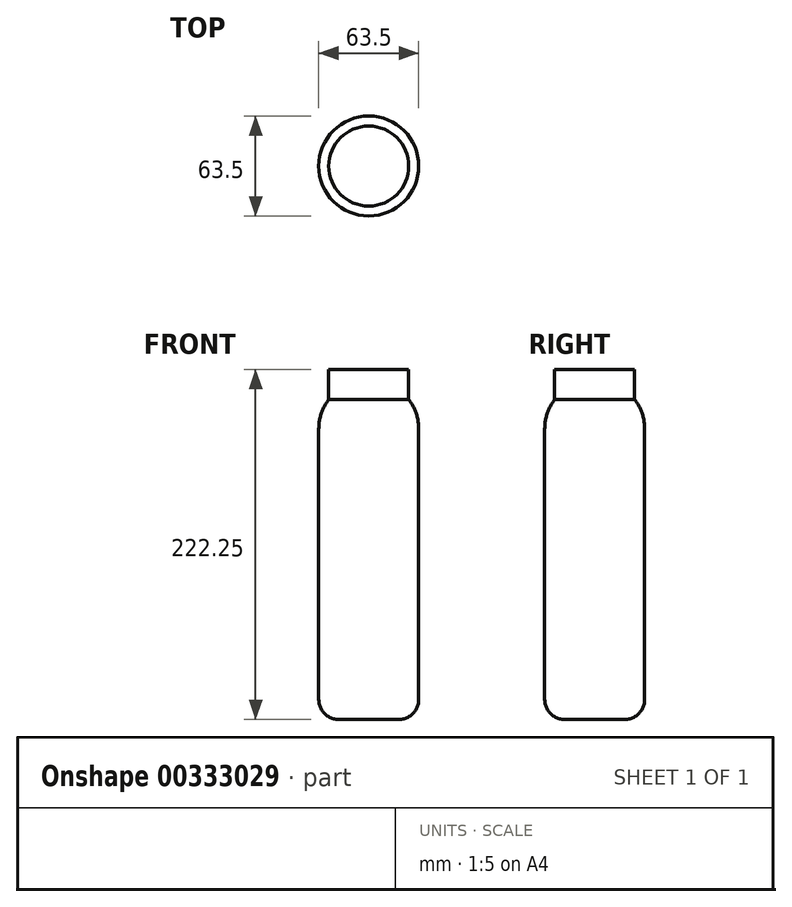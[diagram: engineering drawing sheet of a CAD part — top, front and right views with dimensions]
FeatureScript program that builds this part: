
annotation { "Feature Type Name" : "Feature", "Feature Type Description" : "" }
export const myFeature = defineFeature(function(context is Context, id is Id, definition is map)
    precondition{}
    {
        {
            var Q0;
            Q0=qCreatedBy(makeId("Top.planeOp"),FACE);
            var sketch = newSketch(context, id + "F0", { "sketchPlane" : qUnion([Q0])});
            skCircle(sketch, "E0", {"center": v(0, 0) * mm, "radius": 25.4 * mm});
            skSolve(sketch);
        }
        {
            var Q0;
            Q0 = qSketchRegion(id + "F0", true);
            extrude(context, id + "F1", {"entities" : qUnion([Q0]), "oppositeDirection" : true, "depth" : 19.05 * mm});
        }
        {
            var Q0;
            Q0=makeQuery(id+"F1.opExtrude","CAP_FACE",FACE,{"disambiguationData":[OSD([sQuery(id+"F0.wireOp",EDGE,"E0")])],"isStart":false});
            var sketch = newSketch(context, id + "F2", { "sketchPlane" : qUnion([Q0])});
            skCircle(sketch, "E1", {"center": v(0, 0) * mm, "radius": 31.75 * mm});
            skSolve(sketch);
        }
        {
            var Q0;
            Q0 = qSketchRegion(id + "F2", true);
            extrude(context, id + "F3", {"entities" : qUnion([Q0]), "operationType" : NewBodyOperationType.ADD, "depth" : 203.2 * mm});
        }
        {
            var Q0;
            Q0=makeQuery(id+"F3.opExtrude","CAP_EDGE",EDGE,{"disambiguationData":[OSD([sQuery(id+"F2.wireOp",EDGE,"E1")])],"isStart":false});
            fillet(context, id + "F4", {"entities" : qUnion([Q0]), "radius" : 12.7 * mm, "tangentPropagation" : true, "allowEdgeOverflow" : false});
        }
        {
            var Q0;
            Q0=makeQuery(id+"F3.opExtrude","CAP_EDGE",EDGE,{"disambiguationData":[OSD([sQuery(id+"F2.wireOp",EDGE,"E1")])],"isStart":true});
            fillet(context, id + "F5", {"entities" : qUnion([Q0]), "radius" : 30.48 * mm, "tangentPropagation" : true, "allowEdgeOverflow" : false});
        }
    });
